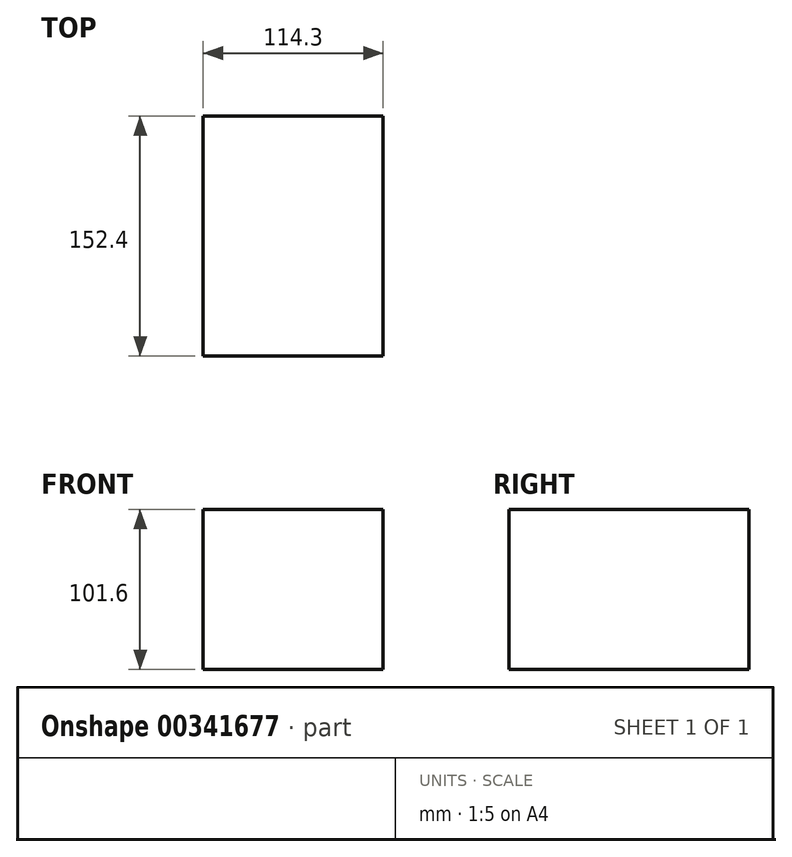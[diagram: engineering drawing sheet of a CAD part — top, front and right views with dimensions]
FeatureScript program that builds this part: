
annotation { "Feature Type Name" : "Feature", "Feature Type Description" : "" }
export const myFeature = defineFeature(function(context is Context, id is Id, definition is map)
    precondition{}
    {
        {
            var Q0;
            Q0=qCreatedBy(makeId("Front.planeOp"),FACE);
            var sketch = newSketch(context, id + "F0", { "sketchPlane" : qUnion([Q0])});
            skLineSegment(sketch, "E0.bottom", {"start": v(-39.14, 52.69) * mm, "end": v(75.16, 52.69) * mm});
            skLineSegment(sketch, "E0.top", {"start": v(-39.14, -48.91) * mm, "end": v(75.16, -48.91) * mm});
            skLineSegment(sketch, "E0.left", {"start": v(-39.14, 52.69) * mm, "end": v(-39.14, -48.91) * mm});
            skLineSegment(sketch, "E0.right", {"start": v(75.16, 52.69) * mm, "end": v(75.16, -48.91) * mm});
            skSolve(sketch);
        }
        {
            var Q0;
            Q0=makeQuery(id+"F0.imprint","IMPRINT",FACE,{"disambiguationData":[TD([[makeQuery(id+"F0.imprint","IMPRINT",EDGE,{"derivedFrom":sQuery(id+"F0.wireOp",EDGE,"E0.bottom")}),-1.0]])]});
            extrude(context, id + "F1", {"entities" : qUnion([Q0]), "depth" : 152.4 * mm, "offsetDistance" : 25.4 * mm});
        }
    });
